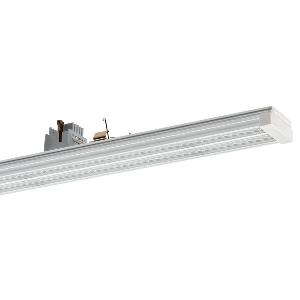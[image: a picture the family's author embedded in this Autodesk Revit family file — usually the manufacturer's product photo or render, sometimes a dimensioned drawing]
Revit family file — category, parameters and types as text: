
# Revit family: conveo_-_cvg_15000_850_xn-l_ea_5_226848489-00804987_58ed
name_source: partatom
category: Lighting Fixtures
units: mm (PartAtom-declared; Revit-internal decimal feet)

## family parameters
Cut with Voids When Loaded = No
Host = Face
Light Source = No
Part Type = Normal
Room Calculation Point = No
Round Connector Dimension = Use Diameter
Shared = No

## types (1)
- CONVEO - CVG 15000/850/xN-L/EA/5 (1 x LED, 15400 lm, 5000K)
    Apparent Load = 95 VA
    Approval mark = CE
    CIE Flux Codes = 86 95 99 100 100
    Color Rendering = 80-89
    Color Temperature = 5000K
    Control Gear = Electronic ballast
    Default Elevation = 1800 mm
    Description = CVG 15000/850/xN-L/EA/5|Continuous-row system|light source: LED|work equipment: Electronic ballast|connected load: 220-240 V, 50-60 Hz|Power consumption: approx. 95 W|luminous flux: 15400 lm|luminous efficacy: 162 lm/W|colour temperature: Cold white, ca. 5000 K|color rendering index (CRI): >= 80|chromaticity tolerance:  3 SDCM|System of protection: IP 54|class of protection: I|technology: Switchable|luminaire body|material: Aluminium|surface: Powder coatet|colour: White|lamp cover: Acrylic (PMMA), Satine|weight (net): approx. 2.2 kg|Fastening: Available separately|maximum ambient temperature: 41 ░C|glare control: Lens optics|Approval mark: VDE - ENEC|
    Frequency = 50 Hz
    Height = 70 mm
    Lamp = 1 x LED
    Lamp Light Flux = 15400 lm
    Lamp count = 1
    Length = 1500 mm
    Luminous efficacy = 162 lm/W
    Manufacturer = Waldmann
    ModVariant = No
    Model = 226848489-00804987
    Mounting Place = Ceiling
    Mounting Type = Pendant
    Number of Poles = 1
    OnlyDefault = Yes
    Power Factor = 1
    Product Name = CONVEO - CVG 15000/850/xN-L/EA/5
    Product group = Continuous-row system (industry)
    ProductGroupID = 301
    Protection Class = Protection class I
    Protection Degree = IP 54
    RLX_Detail_Level = 1
    RlxData = <blob elided: 135225 chars, md5=c823609e>
    Socket = socket
    Standby Power = 0 W
    System Light Flux = 15400 lm
    System Power = 95 W
    Type Comments = Product without accessories
    Type Image = 226848359-00804974-2l5.jpg
    URL = http://relux.com
    VarID = ---
    Voltage = 230 V
    Voltage Range = 220-240 V
    Weight = 0.00 kg
    Width = 64 mm

## geometry (parser evidence)
native form markers: Blend x4, Sweep x9
no freeform markers — native parametric forms only
